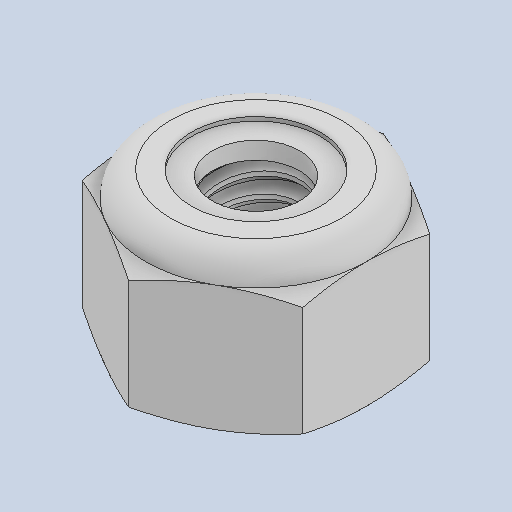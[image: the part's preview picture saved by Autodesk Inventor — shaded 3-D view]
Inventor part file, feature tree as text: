
AUTODESK INVENTOR PART (.ipt)
format: ipt  version: 2024 (Build 280153000, 153)  size: 282,624 bytes
history: native  units: in
note: dims shown in document units (in); Inventor stores cm internally (conversion verified against a paired STEP export)
features: other x2, revolve x1
ambient origin geometry x8: Origin, YZ Plane, XZ Plane, XY Plane, X Axis, Y Axis, Z Axis, Center Point
bodies: Solid1 (feature_tree), Solid2 (feature_tree)
feature tree (3):
  other  "90631A009_Low-Strength Steel Nylon-Insert Locknut1"
  other  "Cut-Revolve4"
  revolve  "Revolve2"  [1 undecoded]
note: 1 required parameter value undecoded (feature->parameter linkage not recoverable at this tier; creation-order binding heuristic only, values carry confidence <= 0.55)
